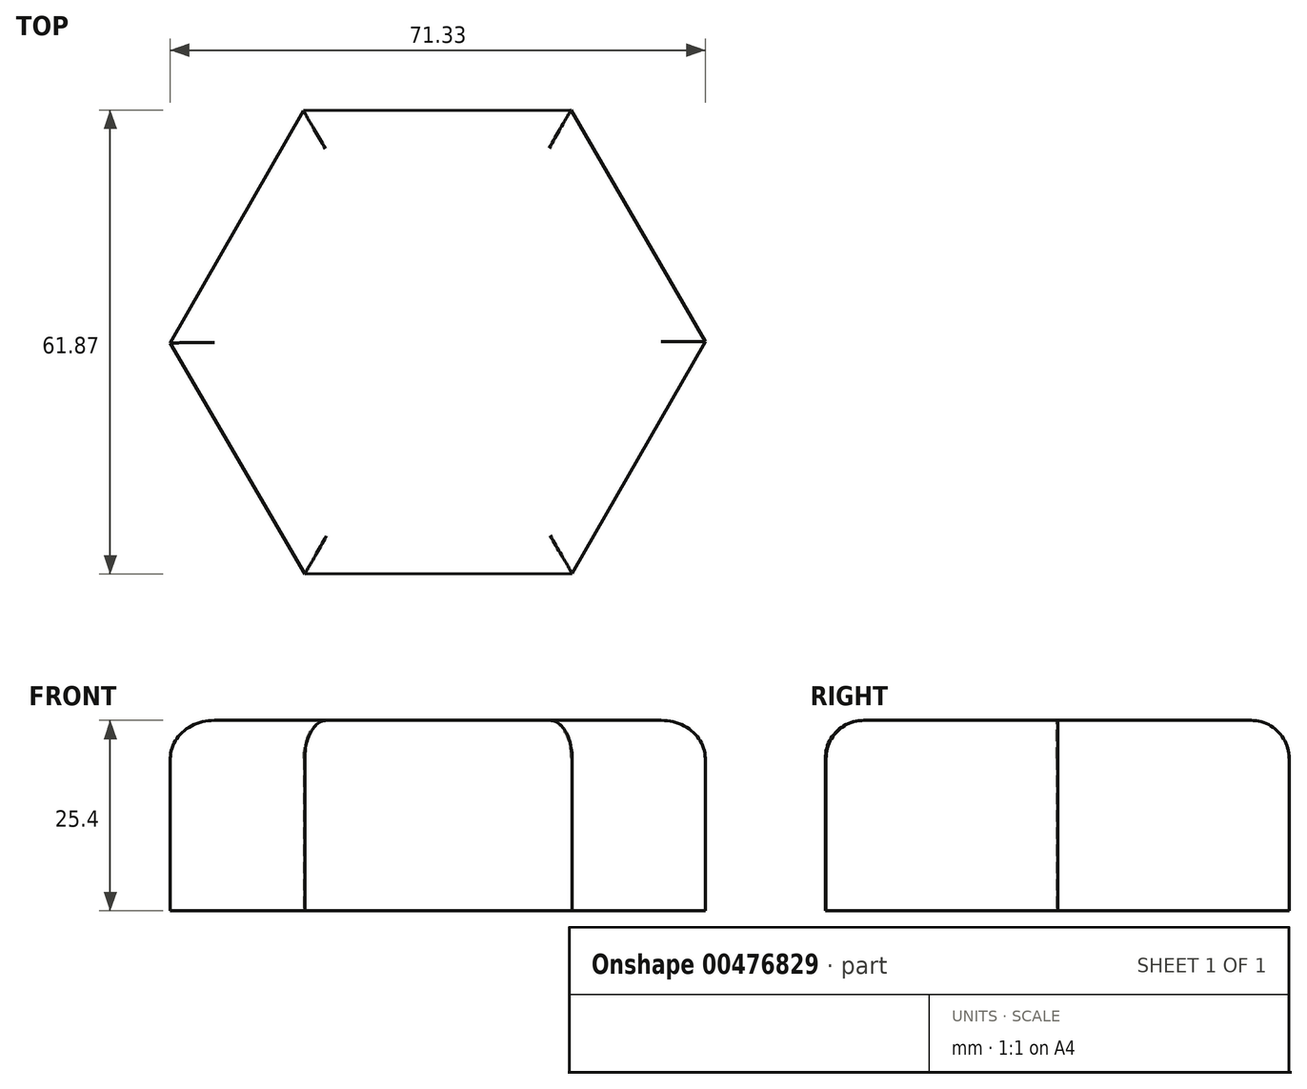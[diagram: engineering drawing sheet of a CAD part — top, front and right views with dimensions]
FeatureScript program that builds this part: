
annotation { "Feature Type Name" : "Feature", "Feature Type Description" : "" }
export const myFeature = defineFeature(function(context is Context, id is Id, definition is map)
    precondition{}
    {
        {
            var Q0;
            Q0=qCreatedBy(makeId("Top.planeOp"),FACE);
            var sketch = newSketch(context, id + "F0", { "sketchPlane" : qUnion([Q0])});
            skCircle(sketch, "E0.cCircle", {"center": v(-9.4, 15.27) * mm, "radius": 35.66 * mm, "construction": true});
            skLineSegment(sketch, "E0.0", {"start": v(8.52, -15.57) * mm, "end": v(-27.15, -15.66) * mm});
            skLineSegment(sketch, "E0.1", {"start": v(-27.15, -15.66) * mm, "end": v(-45.06, 15.18) * mm});
            skLineSegment(sketch, "E0.2", {"start": v(-45.06, 15.18) * mm, "end": v(-27.31, 46.1) * mm});
            skLineSegment(sketch, "E0.3", {"start": v(-27.31, 46.1) * mm, "end": v(8.35, 46.2) * mm});
            skLineSegment(sketch, "E0.4", {"start": v(8.35, 46.2) * mm, "end": v(26.27, 15.37) * mm});
            skLineSegment(sketch, "E0.5", {"start": v(26.27, 15.37) * mm, "end": v(8.52, -15.57) * mm});
            skSolve(sketch);
        }
        {
            var Q0;
            Q0=makeQuery(id+"F0.imprint","IMPRINT",FACE,{"disambiguationData":[TD([[makeQuery(id+"F0.imprint","IMPRINT",EDGE,{"derivedFrom":sQuery(id+"F0.wireOp",EDGE,"E0.0")}),-1.0]])]});
            extrude(context, id + "F1", {"entities" : qUnion([Q0]), "depth" : 25.4 * mm});
        }
        {
            var Q0;
            Q0=makeQuery(id+"F1.opExtrude","CAP_EDGE",EDGE,{"disambiguationData":[OSD([sQuery(id+"F0.wireOp",EDGE,"E0.2")])],"isStart":false});
            var Q1;
            Q1=makeQuery(id+"F1.opExtrude","CAP_EDGE",EDGE,{"disambiguationData":[OSD([sQuery(id+"F0.wireOp",EDGE,"E0.3")])],"isStart":false});
            var Q2;
            Q2=makeQuery(id+"F1.opExtrude","CAP_EDGE",EDGE,{"disambiguationData":[OSD([sQuery(id+"F0.wireOp",EDGE,"E0.4")])],"isStart":false});
            var Q3;
            Q3=makeQuery(id+"F1.opExtrude","CAP_EDGE",EDGE,{"disambiguationData":[OSD([sQuery(id+"F0.wireOp",EDGE,"E0.5")])],"isStart":false});
            var Q4;
            Q4=makeQuery(id+"F1.opExtrude","CAP_EDGE",EDGE,{"disambiguationData":[OSD([sQuery(id+"F0.wireOp",EDGE,"E0.0")])],"isStart":false});
            var Q5;
            Q5=makeQuery(id+"F1.opExtrude","CAP_EDGE",EDGE,{"disambiguationData":[OSD([sQuery(id+"F0.wireOp",EDGE,"E0.1")])],"isStart":false});
            fillet(context, id + "F2", {"entities" : qUnion([Q0, Q1, Q2, Q3, Q4, Q5]), "radius" : 5.08 * mm, "tangentPropagation" : true, "allowEdgeOverflow" : false});
        }
    });
